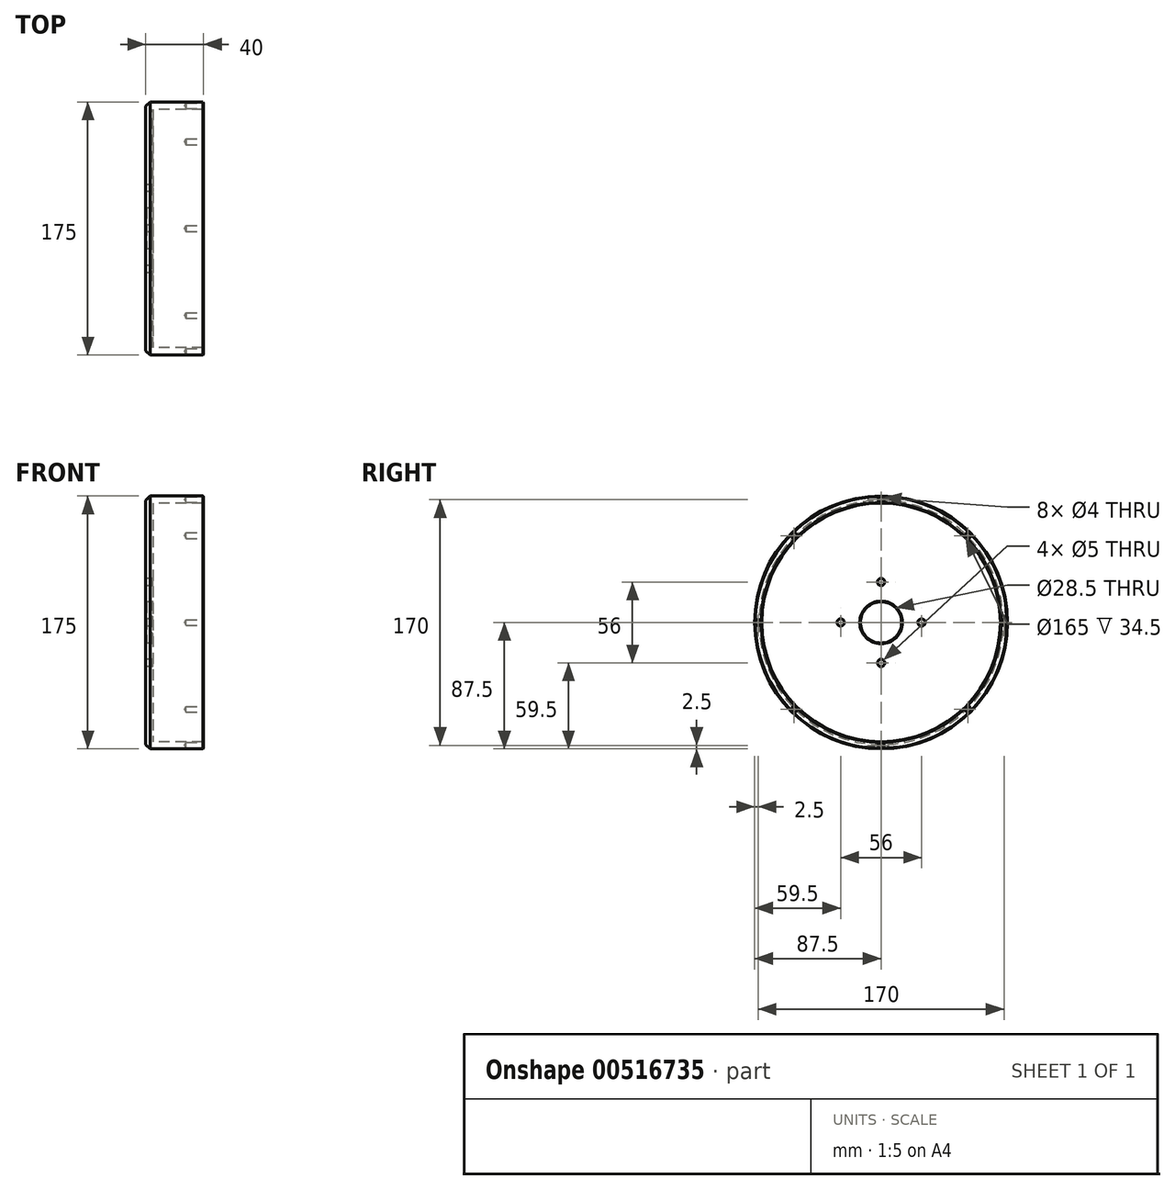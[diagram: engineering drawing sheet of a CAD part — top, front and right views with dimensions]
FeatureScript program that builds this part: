
annotation { "Feature Type Name" : "Feature", "Feature Type Description" : "" }
export const myFeature = defineFeature(function(context is Context, id is Id, definition is map)
    precondition{}
    {
        {
            var Q0;
            Q0=qCreatedBy(makeId("Front.planeOp"),FACE);
            var sketch = newSketch(context, id + "F0", { "sketchPlane" : qUnion([Q0])});
            skLineSegment(sketch, "E0", {"start": v(0, 14.25) * mm, "end": v(0, 87.5) * mm});
            skLineSegment(sketch, "E1", {"start": v(0, 87.5) * mm, "end": v(40, 87.5) * mm});
            skLineSegment(sketch, "E2", {"start": v(40, 87.5) * mm, "end": v(40, 82.5) * mm});
            skLineSegment(sketch, "E3", {"start": v(40, 82.5) * mm, "end": v(5, 82.5) * mm});
            skLineSegment(sketch, "E4", {"start": v(5, 82.5) * mm, "end": v(5, 14.25) * mm});
            skLineSegment(sketch, "E5", {"start": v(5, 14.25) * mm, "end": v(0, 14.25) * mm});
            skLineSegment(sketch, "E6", {"start": v(-40.37, 0) * mm, "end": v(71.78, 0) * mm, "construction": true});
            skSolve(sketch);
        }
        {
            var Q0;
            Q0 = qSketchRegion(id + "F0", true);
            var Q1;
            Q1=sQuery(id+"F0.wireOp",EDGE,"E6");
            revolve(context, id + "F1", {"entities" : qUnion([Q0]), "axis" : qUnion([Q1]), "revolveType" : RevolveType.FULL});
        }
        {
            var Q0;
            Q0=makeQuery(id+"F1.opRevolve","SWEPT_EDGE",EDGE,{"disambiguationData":[OSD([sQuery(id+"F0.wireOp",EDGE,"E0"),sQuery(id+"F0.wireOp",EDGE,"E1")])]});
            chamfer(context, id + "F2", {"entities" : qUnion([Q0]), "width" : 3 * mm, "tangentPropagation" : true});
        }
        {
            var Q0;
            Q0=makeQuery(id+"F1.opRevolve","SWEPT_EDGE",EDGE,{"disambiguationData":[OSD([sQuery(id+"F0.wireOp",EDGE,"E1"),sQuery(id+"F0.wireOp",EDGE,"E2")])]});
            var Q1;
            Q1=makeQuery(id+"F1.opRevolve","SWEPT_EDGE",EDGE,{"disambiguationData":[OSD([sQuery(id+"F0.wireOp",EDGE,"E2"),sQuery(id+"F0.wireOp",EDGE,"E3")])]});
            var Q2;
            Q2=makeQuery(id+"F1.opRevolve","SWEPT_EDGE",EDGE,{"disambiguationData":[OSD([sQuery(id+"F0.wireOp",EDGE,"E4"),sQuery(id+"F0.wireOp",EDGE,"E5")])]});
            var Q3;
            Q3=makeQuery(id+"F1.opRevolve","SWEPT_EDGE",EDGE,{"disambiguationData":[OSD([sQuery(id+"F0.wireOp",EDGE,"E0"),sQuery(id+"F0.wireOp",EDGE,"E5")])]});
            chamfer(context, id + "F3", {"entities" : qUnion([Q0, Q1, Q2, Q3]), "width" : .5 * mm, "tangentPropagation" : true});
        }
        {
            var Q0;
            Q0=makeQuery(id+"F1.opRevolve","SWEPT_FACE",FACE,{"disambiguationData":[OSD([sQuery(id+"F0.wireOp",EDGE,"E0")])]});
            var sketch = newSketch(context, id + "F4", { "sketchPlane" : qUnion([Q0])});
            skCircle(sketch, "E7", {"center": v(0, 0) * mm, "radius": 28 * mm, "construction": true});
            skPoint(sketch, "E8", {"position": v(0, 28) * mm});
            skPoint(sketch, "E9", {"position": v(-28, 0) * mm});
            skPoint(sketch, "E10", {"position": v(0, -28) * mm});
            skPoint(sketch, "E11", {"position": v(28, 0) * mm});
            skSolve(sketch);
        }
        {
            var Q0;
            Q0=sQuery(id+"F4.wireOp",VERTEX,"E8");
            var Q1;
            Q1=sQuery(id+"F4.wireOp",VERTEX,"E9");
            var Q2;
            Q2=sQuery(id+"F4.wireOp",VERTEX,"E10");
            var Q3;
            Q3=sQuery(id+"F4.wireOp",VERTEX,"E11");
            var Q4;
            Q4=makeQuery(id+"F1.opRevolve","SWEPT_BODY",BODY,{"disambiguationData":[OSD([sQuery(id+"F0.wireOp",EDGE,"E0"),sQuery(id+"F0.wireOp",EDGE,"E1"),sQuery(id+"F0.wireOp",EDGE,"E2"),sQuery(id+"F0.wireOp",EDGE,"E3"),sQuery(id+"F0.wireOp",EDGE,"E4"),sQuery(id+"F0.wireOp",EDGE,"E5")])]});
            hole(context, id + "F5", {"style" : HoleStyle.SIMPLE, "endStyle" : HoleEndStyle.THROUGH, "holeDiameter" : 5 * mm, "isTappedThrough" : true, "tappedDepth" : 12 * mm, "tapClearance" : 3, "locations" : qUnion([Q0, Q1, Q2, Q3]), "scope" : qUnion([Q4])});
        }
        {
            var Q0;
            Q0=makeQuery(id+"F1.opRevolve","SWEPT_FACE",FACE,{"disambiguationData":[OSD([sQuery(id+"F0.wireOp",EDGE,"E2")])]});
            var sketch = newSketch(context, id + "F6", { "sketchPlane" : qUnion([Q0])});
            skCircle(sketch, "E12", {"center": v(0, 0) * mm, "radius": 85 * mm, "construction": true});
            skPoint(sketch, "E13", {"position": v(0, 85) * mm});
            skPoint(sketch, "E14.1.0", {"position": v(-60.1, 60.1) * mm});
            skPoint(sketch, "E14.2.0", {"position": v(-85, 0) * mm});
            skPoint(sketch, "E14.3.0", {"position": v(-60.1, -60.1) * mm});
            skPoint(sketch, "E14.4.0", {"position": v(0, -85) * mm});
            skPoint(sketch, "E14.5.0", {"position": v(60.1, -60.1) * mm});
            skPoint(sketch, "E14.6.0", {"position": v(85, 0) * mm});
            skPoint(sketch, "E14.7.0", {"position": v(60.1, 60.1) * mm});
            skLineSegment(sketch, "E14.anchor1", {"start": v(0, 0) * mm, "end": v(0, 85) * mm, "construction": true});
            skLineSegment(sketch, "E14.anchor2", {"start": v(0, 0) * mm, "end": v(60.1, 60.1) * mm, "construction": true});
            skSolve(sketch);
        }
        {
            var Q0;
            Q0=sQuery(id+"F6.wireOp",VERTEX,"E13");
            var Q1;
            Q1=sQuery(id+"F6.wireOp",VERTEX,"E14.2.0");
            var Q2;
            Q2=sQuery(id+"F6.wireOp",VERTEX,"E14.1.0");
            var Q3;
            Q3=sQuery(id+"F6.wireOp",VERTEX,"E14.3.0");
            var Q4;
            Q4=sQuery(id+"F6.wireOp",VERTEX,"E14.4.0");
            var Q5;
            Q5=sQuery(id+"F6.wireOp",VERTEX,"E14.5.0");
            var Q6;
            Q6=sQuery(id+"F6.wireOp",VERTEX,"E14.6.0");
            var Q7;
            Q7=sQuery(id+"F6.wireOp",VERTEX,"E14.7.0");
            var Q8;
            Q8=makeQuery(id+"F1.opRevolve","SWEPT_BODY",BODY,{"disambiguationData":[OSD([sQuery(id+"F0.wireOp",EDGE,"E0"),sQuery(id+"F0.wireOp",EDGE,"E1"),sQuery(id+"F0.wireOp",EDGE,"E2"),sQuery(id+"F0.wireOp",EDGE,"E3"),sQuery(id+"F0.wireOp",EDGE,"E4"),sQuery(id+"F0.wireOp",EDGE,"E5")])]});
            hole(context, id + "F7", {"style" : HoleStyle.SIMPLE, "endStyle" : HoleEndStyle.BLIND, "holeDiameter" : 4 * mm, "holeDepth" : 12 * mm, "isTappedThrough" : true, "tappedDepth" : 12 * mm, "tapClearance" : 3, "locations" : qUnion([Q0, Q1, Q2, Q3, Q4, Q5, Q6, Q7]), "scope" : qUnion([Q8])});
        }
    });
